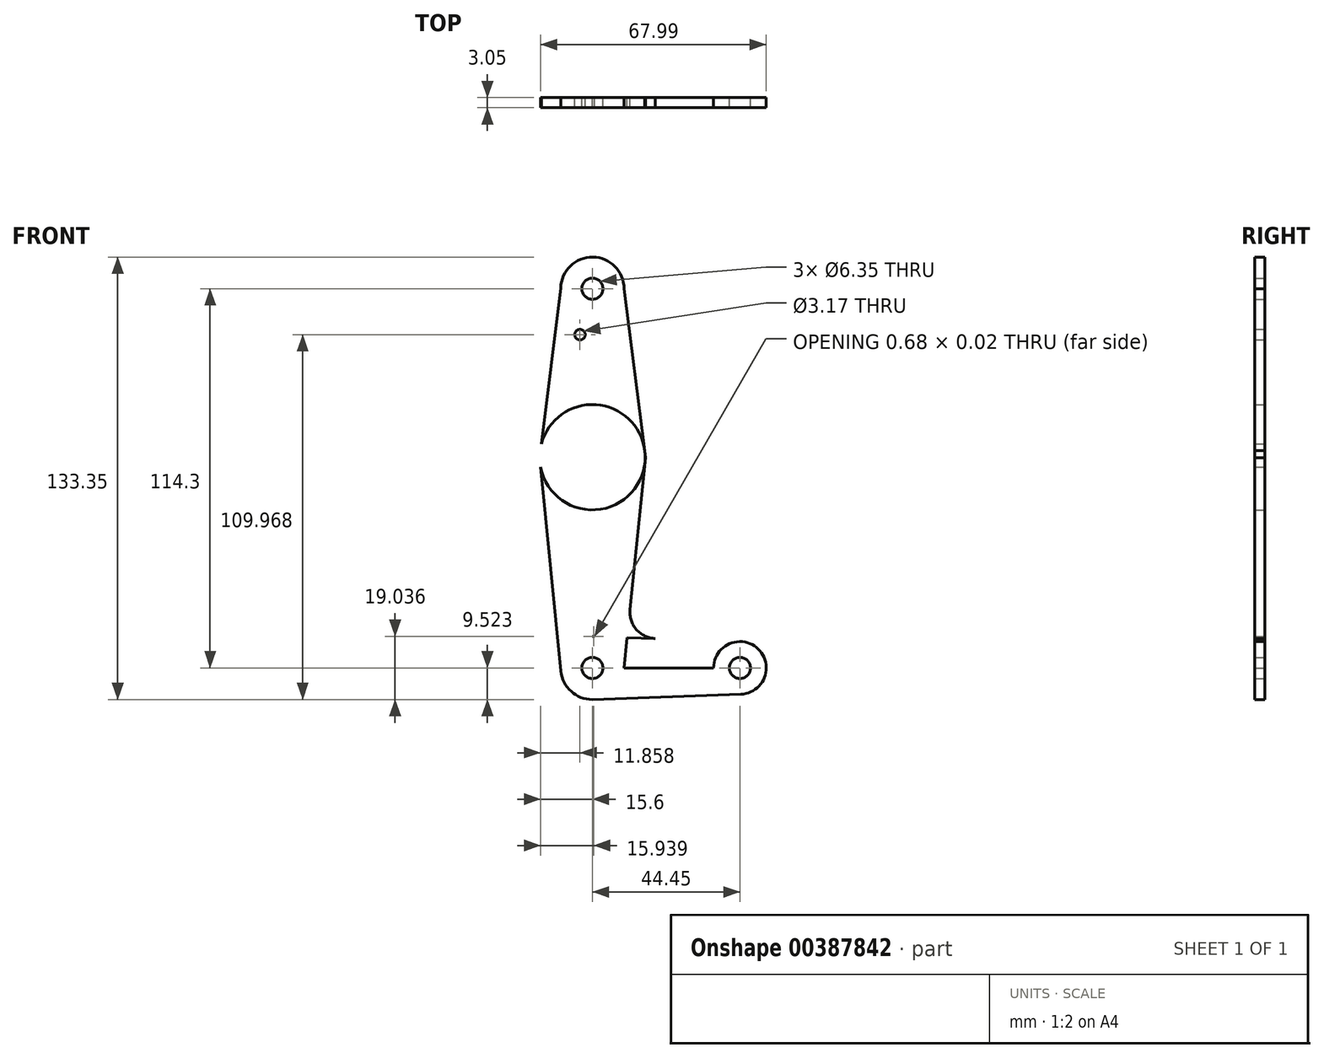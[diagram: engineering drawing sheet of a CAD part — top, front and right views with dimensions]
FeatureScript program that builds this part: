
annotation { "Feature Type Name" : "Feature", "Feature Type Description" : "" }
export const myFeature = defineFeature(function(context is Context, id is Id, definition is map)
    precondition{}
    {
        {
            var Q0;
            Q0=qCreatedBy(makeId("Front.planeOp"),FACE);
            var sketch = newSketch(context, id + "F0", { "sketchPlane" : qUnion([Q0])});
            skLineSegment(sketch, "E0", {"start": v(0, -55.55) * mm, "end": v(0, 58.75) * mm});
            skLineSegment(sketch, "E1", {"start": v(0, 58.75) * mm, "end": v(0, -55.55) * mm});
            skLineSegment(sketch, "E2", {"start": v(0, -55.55) * mm, "end": v(44.45, -55.55) * mm});
            skLineSegment(sketch, "E3", {"start": v(44.45, -55.55) * mm, "end": v(0, -55.55) * mm});
            skCircle(sketch, "E4", {"center": v(0, 58.75) * mm, "radius": 9.53 * mm});
            skLineSegment(sketch, "E5", {"start": v(0, -55.55) * mm, "end": v(0, 7.95) * mm});
            skPoint(sketch, "E6", {"position": v(0, 7.95) * mm});
            skCircle(sketch, "E7", {"center": v(0, 7.95) * mm, "radius": 15.88 * mm});
            skCircle(sketch, "E8", {"center": v(0, -55.55) * mm, "radius": 9.53 * mm});
            skCircle(sketch, "E9", {"center": v(44.45, -55.55) * mm, "radius": 7.94 * mm});
            skLineSegment(sketch, "E10", {"start": v(-9.52, 59.02) * mm, "end": v(-15.87, 7.75) * mm});
            skLineSegment(sketch, "E11", {"start": v(-15.87, 7.75) * mm, "end": v(-9.52, 59.02) * mm});
            skLineSegment(sketch, "E12", {"start": v(9.53, 58.75) * mm, "end": v(16.03, 7.75) * mm});
            skLineSegment(sketch, "E13", {"start": v(16.03, 7.75) * mm, "end": v(11.33, -37.94) * mm});
            skLineSegment(sketch, "E14", {"start": v(9.52, -55.55) * mm, "end": v(16.03, 7.75) * mm});
            skLineSegment(sketch, "E15", {"start": v(-15.87, 7.75) * mm, "end": v(-9.48, -56.5) * mm});
            skLineSegment(sketch, "E16", {"start": v(-9.48, -56.5) * mm, "end": v(-15.87, 7.75) * mm});
            skLineSegment(sketch, "E17", {"start": v(0, -46.02) * mm, "end": v(44.73, -47.61) * mm});
            skLineSegment(sketch, "E18", {"start": v(44.73, -47.61) * mm, "end": v(18.96, -46.7) * mm});
            skLineSegment(sketch, "E19", {"start": v(0, -65.07) * mm, "end": v(44.73, -63.48) * mm});
            skCircle(sketch, "E20", {"center": v(-3.74, 44.9) * mm, "radius": 1.59 * mm});
            skCircle(sketch, "E21", {"center": v(0, 58.75) * mm, "radius": 3.18 * mm});
            skCircle(sketch, "E22", {"center": v(0, 7.95) * mm, "radius": 3.18 * mm});
            skCircle(sketch, "E23", {"center": v(0, -55.55) * mm, "radius": 3.18 * mm});
            skCircle(sketch, "E24", {"center": v(44.45, -55.55) * mm, "radius": 3.18 * mm});
            skArc(sketch, "E25.filletArc", {"start": v(11.33, -37.94) * mm, "mid": v(13.25, -43.97) * mm, "end": v(18.96, -46.7) * mm});
            skSolve(sketch);
        }
        {
            var Q0;
            Q0=makeQuery(id+"F0.imprint","IMPRINT",FACE,{"disambiguationData":[TD([[makeQuery(id+"F0.imprint","IMPRINT",EDGE,{"derivedFrom":sQuery(id+"F0.wireOp",EDGE,"E20")}),-1.0]])]});
            var Q1;
            {var subQ0=sQuery(id+"F0.wireOp",EDGE,"E4");var subQ1=sQuery(id+"F0.wireOp",EDGE,"E1");var subQ2=makeQuery(id+"F0.imprint","INTERSECT",VERTEX,{"derivedFrom":[subQ1,subQ0]});Q1=makeQuery(id+"F0.imprint","IMPRINT",FACE,{"disambiguationData":[TD([[makeQuery(id+"F0.imprint","IMPRINT",EDGE,{"disambiguationData":[TD([[subQ2,-1.0]])],"derivedFrom":subQ1}),1.0]])]});}
            var Q2;
            Q2=makeQuery(id+"F0.imprint","IMPRINT",FACE,{"disambiguationData":[TD([[makeQuery(id+"F0.imprint","IMPRINT",EDGE,{"derivedFrom":sQuery(id+"F0.wireOp",EDGE,"E21")}),-1.0]])]});
            var Q3;
            {var subQ1=sQuery(id+"F0.wireOp",EDGE,"E7");var subQ8=sQuery(id+"F0.wireOp",EDGE,"E1");var subQ9=makeQuery(id+"F0.imprint","INTERSECT",VERTEX,{"derivedFrom":[subQ8,subQ1]});Q3=makeQuery(id+"F0.imprint","IMPRINT",FACE,{"disambiguationData":[TD([[makeQuery(id+"F0.imprint","IMPRINT",EDGE,{"disambiguationData":[TD([[subQ9,-1.0]])],"derivedFrom":subQ8}),-1.0]])]});}
            var Q4;
            {var subQ3=sQuery(id+"F0.wireOp",EDGE,"E7");var subQ5=sQuery(id+"F0.wireOp",EDGE,"E16");var subQ7=makeQuery(id+"F0.imprint","INTERSECT",VERTEX,{"derivedFrom":[subQ3,subQ5]});Q4=makeQuery(id+"F0.imprint","IMPRINT",FACE,{"disambiguationData":[TD([[makeQuery(id+"F0.imprint","IMPRINT",EDGE,{"disambiguationData":[TD([[subQ7,-1.0]])],"derivedFrom":subQ3}),-1.0]])]});}
            var Q5;
            {var subQ1=sQuery(id+"F0.wireOp",EDGE,"E12");var subQ3=sQuery(id+"F0.wireOp",EDGE,"E7");var subQ4=makeQuery(id+"F0.imprint","INTERSECT",VERTEX,{"derivedFrom":[subQ3,subQ1]});Q5=makeQuery(id+"F0.imprint","IMPRINT",FACE,{"disambiguationData":[TD([[makeQuery(id+"F0.imprint","IMPRINT",EDGE,{"disambiguationData":[TD([[subQ4,1.0]])],"derivedFrom":subQ3}),-1.0]])]});}
            var Q6;
            {var subQ1=sQuery(id+"F0.wireOp",EDGE,"E8");var subQ3=sQuery(id+"F0.wireOp",EDGE,"E17");var subQ4=makeQuery(id+"F0.imprint","INTERSECT",VERTEX,{"derivedFrom":[subQ1,subQ3]});Q6=makeQuery(id+"F0.imprint","IMPRINT",FACE,{"disambiguationData":[TD([[makeQuery(id+"F0.imprint","IMPRINT",EDGE,{"disambiguationData":[TD([[subQ4,-1.0]])],"derivedFrom":subQ3}),-1.0]])]});}
            var Q7;
            {var subQ0=sQuery(id+"F0.wireOp",EDGE,"E8");var subQ1=makeQuery(id+"F0.imprint","INTERSECT",VERTEX,{"derivedFrom":[subQ0,sQuery(id+"F0.wireOp",EDGE,"E16")]});Q7=makeQuery(id+"F0.imprint","IMPRINT",FACE,{"disambiguationData":[TD([[makeQuery(id+"F0.imprint","IMPRINT",EDGE,{"disambiguationData":[TD([[subQ1,-1.0]])],"derivedFrom":subQ0}),1.0]])]});}
            var Q8;
            {var subQ5=sQuery(id+"F0.wireOp",EDGE,"E3");var subQ7=sQuery(id+"F0.wireOp",EDGE,"E23");var subQ9=makeQuery(id+"F0.imprint","INTERSECT",VERTEX,{"derivedFrom":[subQ5,subQ7]});Q8=makeQuery(id+"F0.imprint","IMPRINT",FACE,{"disambiguationData":[TD([[makeQuery(id+"F0.imprint","IMPRINT",EDGE,{"disambiguationData":[TD([[subQ9,-1.0]])],"derivedFrom":subQ7}),-1.0]])]});}
            var Q9;
            {var subQ0=sQuery(id+"F0.wireOp",EDGE,"E25.filletArc");Q9=makeQuery(id+"F0.imprint","IMPRINT",FACE,{"disambiguationData":[TD([[makeQuery(id+"F0.imprint","IMPRINT",EDGE,{"derivedFrom":subQ0}),-1.0]])]});}
            var Q10;
            {var subQ0=sQuery(id+"F0.wireOp",EDGE,"E18");Q10=makeQuery(id+"F0.imprint","IMPRINT",FACE,{"disambiguationData":[TD([[makeQuery(id+"F0.imprint","IMPRINT",EDGE,{"derivedFrom":subQ0}),1.0]])]});}
            var Q11;
            {var subQ3=sQuery(id+"F0.wireOp",EDGE,"E9");var subQ5=sQuery(id+"F0.wireOp",EDGE,"E19");var subQ6=makeQuery(id+"F0.imprint","INTERSECT",VERTEX,{"derivedFrom":[subQ3,subQ5]});Q11=makeQuery(id+"F0.imprint","IMPRINT",FACE,{"disambiguationData":[TD([[makeQuery(id+"F0.imprint","IMPRINT",EDGE,{"disambiguationData":[TD([[subQ6,1.0]])],"derivedFrom":subQ3}),-1.0]])]});}
            var Q12;
            Q12=makeQuery(id+"F0.imprint","IMPRINT",FACE,{"disambiguationData":[TD([[makeQuery(id+"F0.imprint","IMPRINT",EDGE,{"derivedFrom":sQuery(id+"F0.wireOp",EDGE,"E24")}),-1.0]])]});
            var Q13;
            {var subQ0=sQuery(id+"F0.wireOp",EDGE,"E7");var subQ4=sQuery(id+"F0.wireOp",EDGE,"E1");var subQ5=makeQuery(id+"F0.imprint","INTERSECT",VERTEX,{"derivedFrom":[subQ4,subQ0]});Q13=makeQuery(id+"F0.imprint","IMPRINT",FACE,{"disambiguationData":[TD([[makeQuery(id+"F0.imprint","IMPRINT",EDGE,{"disambiguationData":[TD([[subQ5,-1.0]])],"derivedFrom":subQ4}),1.0]])]});}
            extrude(context, id + "F1", {"entities" : qUnion([Q0, Q1, Q2, Q3, Q4, Q5, Q6, Q7, Q8, Q9, Q10, Q11, Q12, Q13]), "depth" : 3.05 * mm});
        }
    });
